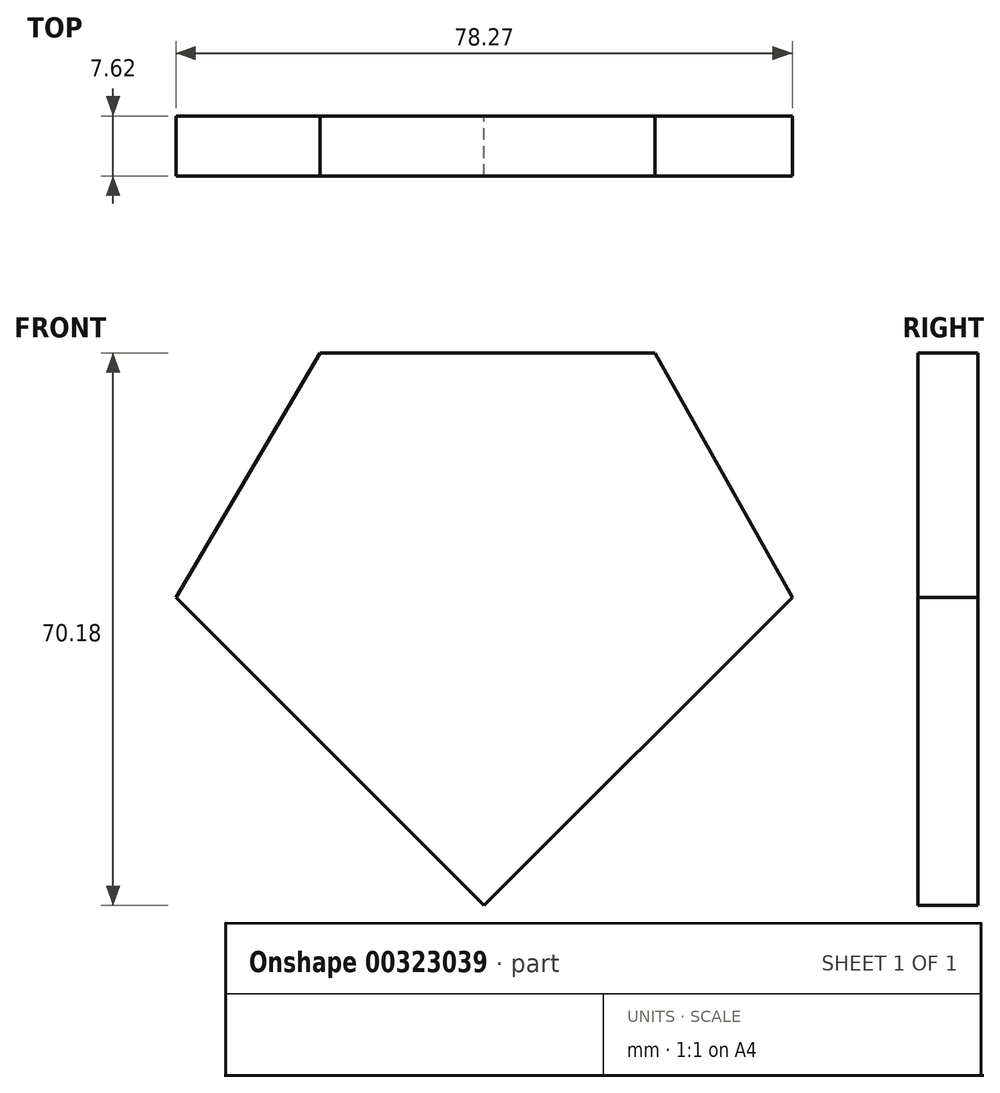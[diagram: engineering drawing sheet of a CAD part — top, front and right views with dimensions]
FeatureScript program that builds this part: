
annotation { "Feature Type Name" : "Feature", "Feature Type Description" : "" }
export const myFeature = defineFeature(function(context is Context, id is Id, definition is map)
    precondition{}
    {
        {
            var Q0;
            Q0=qCreatedBy(makeId("Front.planeOp"),FACE);
            var sketch = newSketch(context, id + "F0", { "sketchPlane" : qUnion([Q0])});
            skLineSegment(sketch, "E0", {"start": v(-20.82, 27.11) * mm, "end": v(21.72, 27.11) * mm});
            skLineSegment(sketch, "E1", {"start": v(21.72, 27.11) * mm, "end": v(39.16, -3.94) * mm});
            skLineSegment(sketch, "E2", {"start": v(39.16, -3.94) * mm, "end": v(0, -43.07) * mm});
            skLineSegment(sketch, "E3", {"start": v(0, -43.07) * mm, "end": v(-39.11, -3.94) * mm});
            skLineSegment(sketch, "E4", {"start": v(-39.11, -3.94) * mm, "end": v(-20.82, 27.11) * mm});
            skLineSegment(sketch, "E5", {"start": v(-39.11, -3.94) * mm, "end": v(39.16, -3.94) * mm});
            skLineSegment(sketch, "E6", {"start": v(-27.2, 16.28) * mm, "end": v(27.8, 16.28) * mm});
            skLineSegment(sketch, "E7", {"start": v(0, 16.28) * mm, "end": v(0, -43.07) * mm});
            skLineSegment(sketch, "E8", {"start": v(17.3, 16.28) * mm, "end": v(17.3, -25.79) * mm});
            skLineSegment(sketch, "E9", {"start": v(-14.89, 16.28) * mm, "end": v(-14.89, -28.17) * mm});
            skSolve(sketch);
        }
        {
            var Q0;
            Q0 = qSketchRegion(id + "F0", true);
            var Q1;
            {var subQ0=sQuery(id+"F0.wireOp",EDGE,"E7");var subQ1=sQuery(id+"F0.wireOp",EDGE,"E5");var subQ2=makeQuery(id+"F0.imprint","INTERSECT",VERTEX,{"derivedFrom":[subQ1,subQ0]});Q1=makeQuery(id+"F0.imprint","IMPRINT",FACE,{"disambiguationData":[TD([[makeQuery(id+"F0.imprint","IMPRINT",EDGE,{"disambiguationData":[TD([[subQ2,-1.0]])],"derivedFrom":subQ1}),1.0]])]});}
            var Q2;
            {var subQ0=sQuery(id+"F0.wireOp",EDGE,"E9");var subQ1=sQuery(id+"F0.wireOp",EDGE,"E5");var subQ2=makeQuery(id+"F0.imprint","INTERSECT",VERTEX,{"derivedFrom":[subQ1,subQ0]});Q2=makeQuery(id+"F0.imprint","IMPRINT",FACE,{"disambiguationData":[TD([[makeQuery(id+"F0.imprint","IMPRINT",EDGE,{"disambiguationData":[TD([[subQ2,-1.0]])],"derivedFrom":subQ1}),1.0]])]});}
            extrude(context, id + "F1", {"entities" : qUnion([Q0, Q1, Q2]), "depth" : 7.62 * mm});
        }
    });
